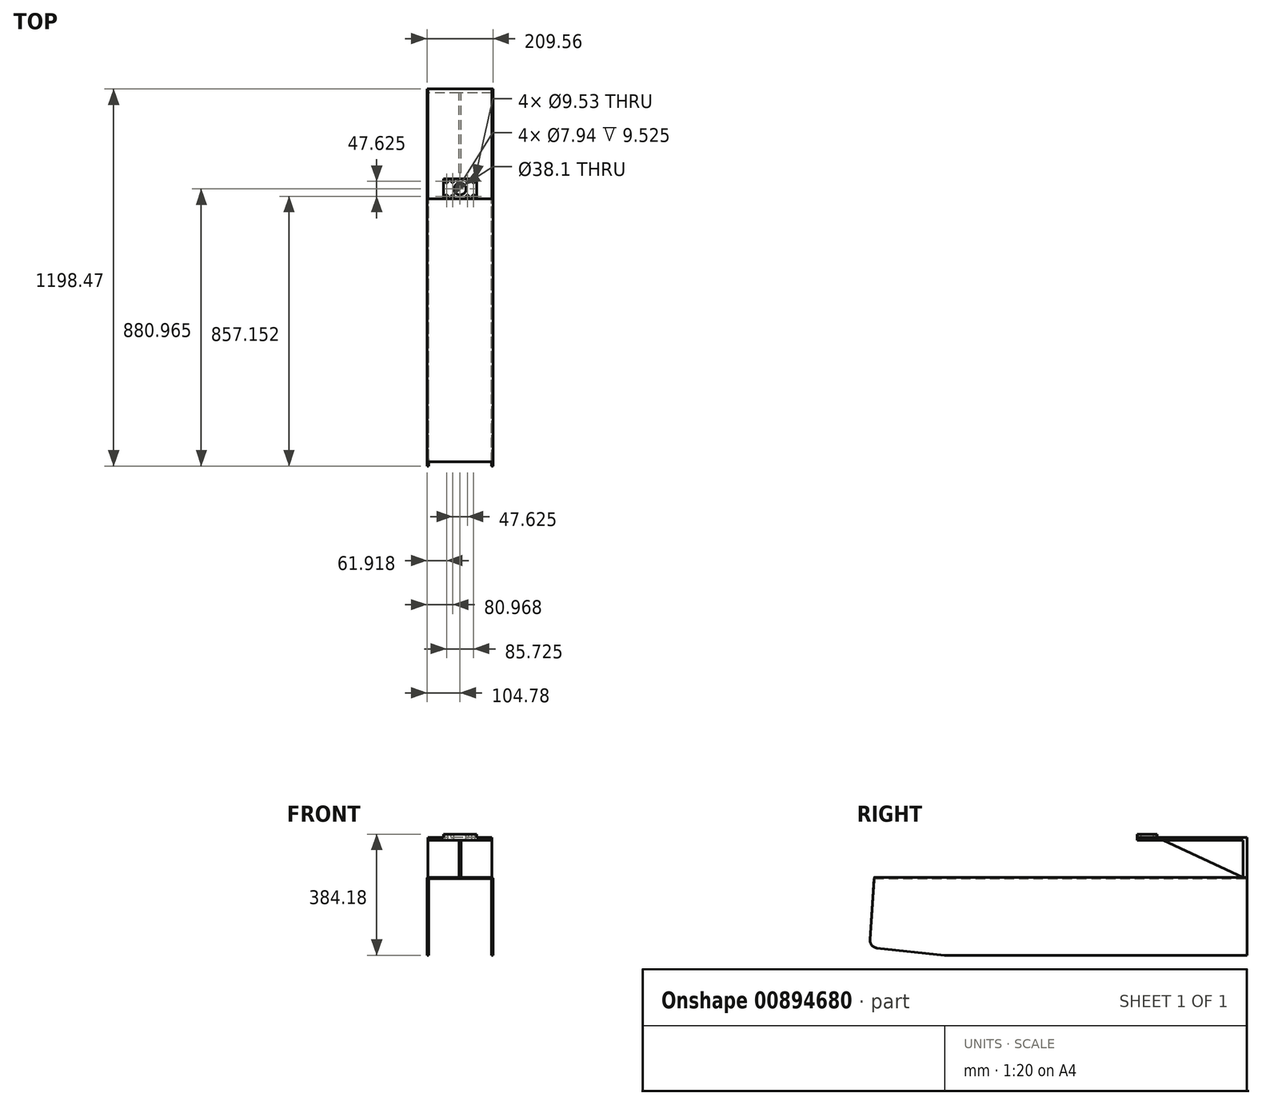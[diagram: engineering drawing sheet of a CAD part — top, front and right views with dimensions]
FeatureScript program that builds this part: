
annotation { "Feature Type Name" : "Feature", "Feature Type Description" : "" }
export const myFeature = defineFeature(function(context is Context, id is Id, definition is map)
    precondition{}
    {
        {
            var Q0;
            Q0=qCreatedBy(makeId("Front.planeOp"),FACE);
            var sketch = newSketch(context, id + "F0", { "sketchPlane" : qUnion([Q0])});
            skLineSegment(sketch, "E0", {"start": v(-100.01, -242.89) * mm, "end": v(-100.01, 0) * mm});
            skLineSegment(sketch, "E1", {"start": v(-100.01, 0) * mm, "end": v(100.01, 0) * mm});
            skLineSegment(sketch, "E2", {"start": v(100.01, 0) * mm, "end": v(100.01, -242.89) * mm});
            skLineSegment(sketch, "E3", {"start": v(-100.01, -242.89) * mm, "end": v(-104.78, -242.89) * mm});
            skLineSegment(sketch, "E4", {"start": v(-104.78, -242.89) * mm, "end": v(-104.78, 4.76) * mm});
            skLineSegment(sketch, "E5", {"start": v(-104.78, 4.76) * mm, "end": v(104.78, 4.76) * mm});
            skLineSegment(sketch, "E6", {"start": v(104.78, 4.76) * mm, "end": v(104.78, -242.89) * mm});
            skLineSegment(sketch, "E7", {"start": v(104.78, -242.89) * mm, "end": v(100.01, -242.89) * mm});
            skSolve(sketch);
        }
        {
            var Q0;
            Q0 = qSketchRegion(id + "F0", true);
            extrude(context, id + "F1", {"entities" : qUnion([Q0]), "endBound" : BoundingType.SYMMETRIC, "depth" : 1200.15 * mm, "offsetDistance" : 25.4 * mm});
        }
        {
            var Q0;
            Q0=makeQuery(id+"F1.opExtrude","SWEPT_EDGE",EDGE,{"disambiguationData":[OSD([sQuery(id+"F0.wireOp",EDGE,"E4"),sQuery(id+"F0.wireOp",EDGE,"E5")])]});
            var Q1;
            Q1=makeQuery(id+"F1.opExtrude","SWEPT_EDGE",EDGE,{"disambiguationData":[OSD([sQuery(id+"F0.wireOp",EDGE,"E0"),sQuery(id+"F0.wireOp",EDGE,"E1")])]});
            var Q2;
            Q2=makeQuery(id+"F1.opExtrude","SWEPT_EDGE",EDGE,{"disambiguationData":[OSD([sQuery(id+"F0.wireOp",EDGE,"E5"),sQuery(id+"F0.wireOp",EDGE,"E6")])]});
            var Q3;
            Q3=makeQuery(id+"F1.opExtrude","SWEPT_EDGE",EDGE,{"disambiguationData":[OSD([sQuery(id+"F0.wireOp",EDGE,"E1"),sQuery(id+"F0.wireOp",EDGE,"E2")])]});
            fillet(context, id + "F2", {"entities" : qUnion([Q0, Q1, Q2, Q3]), "radius" : 4.76 * mm, "tangentPropagation" : true, "allowEdgeOverflow" : false});
        }
        {
            var Q0;
            Q0=makeQuery(id+"F1.opExtrude","SWEPT_FACE",FACE,{"disambiguationData":[OSD([sQuery(id+"F0.wireOp",EDGE,"E4")])]});
            var sketch = newSketch(context, id + "F3", { "sketchPlane" : qUnion([Q0])});
            skLineSegment(sketch, "E8", {"start": v(600.08, -217.49) * mm, "end": v(361.95, -242.89) * mm});
            skLineSegment(sketch, "E9", {"start": v(361.95, -242.89) * mm, "end": v(600.08, -242.89) * mm});
            skLineSegment(sketch, "E10", {"start": v(600.08, -242.89) * mm, "end": v(600.08, -217.49) * mm});
            skLineSegment(sketch, "E11", {"start": v(584.2, 4.76) * mm, "end": v(600.08, 4.76) * mm});
            skSolve(sketch);
        }
        {
            var Q0;
            Q0 = qSketchRegion(id + "F3", true);
            var Q1;
            Q1=makeQuery(id+"F1.opExtrude","SWEPT_FACE",FACE,{"disambiguationData":[OSD([sQuery(id+"F0.wireOp",EDGE,"E6")])]});
            extrude(context, id + "F4", {"entities" : qUnion([Q0]), "operationType" : NewBodyOperationType.REMOVE, "endBound" : BoundingType.UP_TO_SURFACE, "oppositeDirection" : true, "depth" : 25.4 * mm, "endBoundEntityFace" : qUnion([Q1]), "offsetDistance" : 25.4 * mm});
        }
        {
            var Q0;
            Q0=makeQuery(id+"F1.opExtrude","SWEPT_FACE",FACE,{"disambiguationData":[OSD([sQuery(id+"F0.wireOp",EDGE,"E4")])]});
            var sketch = newSketch(context, id + "F5", { "sketchPlane" : qUnion([Q0])});
            skLineSegment(sketch, "E12", {"start": v(600.08, -217.49) * mm, "end": v(600.08, 4.76) * mm});
            skLineSegment(sketch, "E13", {"start": v(600.08, 4.76) * mm, "end": v(584.2, 4.76) * mm});
            skLineSegment(sketch, "E14", {"start": v(584.2, 4.76) * mm, "end": v(600.08, -217.49) * mm});
            skSolve(sketch);
        }
        {
            var Q0;
            Q0 = qSketchRegion(id + "F5", true);
            var Q1;
            Q1=makeQuery(id+"F1.opExtrude","SWEPT_FACE",FACE,{"disambiguationData":[OSD([sQuery(id+"F0.wireOp",EDGE,"E6")])]});
            extrude(context, id + "F6", {"entities" : qUnion([Q0]), "operationType" : NewBodyOperationType.REMOVE, "endBound" : BoundingType.UP_TO_SURFACE, "oppositeDirection" : true, "depth" : 25.4 * mm, "endBoundEntityFace" : qUnion([Q1]), "offsetDistance" : 25.4 * mm});
        }
        {
            var Q0;
            {var subQ0=sQuery(id+"F3.wireOp",EDGE,"E8");var subQ1=sQuery(id+"F0.wireOp",EDGE,"E0");var subQ2=sQuery(id+"F0.wireOp",EDGE,"E4");Q0=makeQuery(id+"F6.boolean.opBoolean","MERGE",EDGE,{"derivedFrom":[makeQuery(id+"F4.boolean.opBoolean","COPY",EDGE,{"disambiguationData":[TD([makeQuery(id+"F1.opExtrude","SWEPT_FACE",FACE,{"disambiguationData":[OSD([subQ1])]})])],"derivedFrom":makeQuery(id+"F4.opExtrude","SWEPT_EDGE",EDGE,{"disambiguationData":[OSD([subQ2,subQ0,sQuery(id+"F3.wireOp",EDGE,"E10")])]})})],"fromTools":[makeQuery(id+"F6.opExtrude","SWEPT_EDGE",EDGE,{"disambiguationData":[OSD([subQ0,sQuery(id+"F5.wireOp",EDGE,"E12"),sQuery(id+"F5.wireOp",EDGE,"E14")])]})]});}
            var Q1;
            {var subQ0=sQuery(id+"F3.wireOp",EDGE,"E8");var subQ2=sQuery(id+"F0.wireOp",EDGE,"E4");var subQ3=sQuery(id+"F0.wireOp",EDGE,"E2");Q1=makeQuery(id+"F6.boolean.opBoolean","MERGE",EDGE,{"derivedFrom":[makeQuery(id+"F4.boolean.opBoolean","COPY",EDGE,{"disambiguationData":[TD([makeQuery(id+"F1.opExtrude","SWEPT_FACE",FACE,{"disambiguationData":[OSD([subQ3])]})])],"derivedFrom":makeQuery(id+"F4.opExtrude","SWEPT_EDGE",EDGE,{"disambiguationData":[OSD([subQ2,subQ0,sQuery(id+"F3.wireOp",EDGE,"E10")])]})})],"fromTools":[makeQuery(id+"F6.opExtrude","SWEPT_EDGE",EDGE,{"disambiguationData":[OSD([subQ0,sQuery(id+"F5.wireOp",EDGE,"E12"),sQuery(id+"F5.wireOp",EDGE,"E14")])]})]});}
            var Q2;
            {var subQ0=sQuery(id+"F0.wireOp",EDGE,"E3");var subQ1=sQuery(id+"F3.wireOp",EDGE,"E8");Q2=makeQuery(id+"F4.boolean.opBoolean","COPY",EDGE,{"disambiguationData":[topologyDisambiguationEdgeConnected([makeQuery(id+"F1.opExtrude","SWEPT_FACE",FACE,{"disambiguationData":[OSD([subQ0])]})])],"derivedFrom":makeQuery(id+"F4.opExtrude","SWEPT_EDGE",EDGE,{"disambiguationData":[OSD([subQ0,sQuery(id+"F0.wireOp",EDGE,"E4"),subQ1,sQuery(id+"F3.wireOp",EDGE,"E9")])]})});}
            var Q3;
            {var subQ0=sQuery(id+"F3.wireOp",EDGE,"E8");Q3=makeQuery(id+"F4.boolean.opBoolean","COPY",EDGE,{"disambiguationData":[topologyDisambiguationEdgeConnected([makeQuery(id+"F1.opExtrude","SWEPT_FACE",FACE,{"disambiguationData":[OSD([sQuery(id+"F0.wireOp",EDGE,"E7")])]})])],"derivedFrom":makeQuery(id+"F4.opExtrude","SWEPT_EDGE",EDGE,{"disambiguationData":[OSD([sQuery(id+"F0.wireOp",EDGE,"E3"),sQuery(id+"F0.wireOp",EDGE,"E4"),subQ0,sQuery(id+"F3.wireOp",EDGE,"E9")])]})});}
            fillet(context, id + "F7", {"entities" : qUnion([Q0, Q1, Q2, Q3]), "radius" : 25.4 * mm, "tangentPropagation" : true, "allowEdgeOverflow" : false});
        }
        {
            var Q0;
            Q0=qCreatedBy(makeId("Right.planeOp"),FACE);
            var sketch = newSketch(context, id + "F8", { "sketchPlane" : qUnion([Q0])});
            skLineSegment(sketch, "E15", {"start": v(600.08, 4.76) * mm, "end": v(600.08, 131.76) * mm});
            skLineSegment(sketch, "E16", {"start": v(600.08, 131.76) * mm, "end": v(250.82, 131.76) * mm});
            skLineSegment(sketch, "E17", {"start": v(250.82, 131.76) * mm, "end": v(250.82, 122.24) * mm});
            skLineSegment(sketch, "E18", {"start": v(250.82, 122.24) * mm, "end": v(587.38, 122.24) * mm});
            skLineSegment(sketch, "E19", {"start": v(587.38, 122.24) * mm, "end": v(587.38, 4.76) * mm});
            skLineSegment(sketch, "E20", {"start": v(587.38, 4.76) * mm, "end": v(600.08, 4.76) * mm});
            skSolve(sketch);
        }
        {
            var Q0;
            Q0 = qSketchRegion(id + "F8", true);
            extrude(context, id + "F9", {"entities" : qUnion([Q0]), "operationType" : NewBodyOperationType.ADD, "endBound" : BoundingType.SYMMETRIC, "depth" : 203.2 * mm, "offsetDistance" : 25.4 * mm});
        }
        {
            var Q0;
            Q0=qCreatedBy(makeId("Right.planeOp"),FACE);
            var sketch = newSketch(context, id + "F10", { "sketchPlane" : qUnion([Q0])});
            skLineSegment(sketch, "E21", {"start": v(587.38, 122.24) * mm, "end": v(587.38, 4.76) * mm});
            skLineSegment(sketch, "E22", {"start": v(587.38, 4.76) * mm, "end": v(333.37, 122.24) * mm});
            skLineSegment(sketch, "E23", {"start": v(333.38, 122.24) * mm, "end": v(587.38, 122.24) * mm});
            skSolve(sketch);
        }
        {
            var Q0;
            Q0 = qSketchRegion(id + "F10", true);
            extrude(context, id + "F11", {"entities" : qUnion([Q0]), "operationType" : NewBodyOperationType.ADD, "endBound" : BoundingType.SYMMETRIC, "depth" : 6.35 * mm, "offsetDistance" : 25.4 * mm});
        }
        {
            var Q0;
            Q0=makeQuery(id+"F9.opExtrude","SWEPT_FACE",FACE,{"disambiguationData":[OSD([sQuery(id+"F8.wireOp",EDGE,"E16")])]});
            var sketch = newSketch(context, id + "F12", { "sketchPlane" : qUnion([Q0])});
            skLineSegment(sketch, "E24.bottom", {"start": v(52.39, 314.32) * mm, "end": v(-52.39, 314.32) * mm});
            skLineSegment(sketch, "E24.top", {"start": v(52.39, 250.82) * mm, "end": v(-52.39, 250.82) * mm});
            skLineSegment(sketch, "E24.left", {"start": v(52.39, 314.32) * mm, "end": v(52.39, 250.82) * mm});
            skLineSegment(sketch, "E24.right", {"start": v(-52.39, 314.32) * mm, "end": v(-52.39, 250.82) * mm});
            skPoint(sketch, "E24.middle", {"position": v(0, 282.57) * mm});
            skSolve(sketch);
        }
        {
            var Q0;
            Q0 = qSketchRegion(id + "F12", true);
            extrude(context, id + "F13", {"entities" : qUnion([Q0]), "operationType" : NewBodyOperationType.ADD, "depth" : 9.52 * mm, "offsetDistance" : 25.4 * mm});
        }
        {
            var Q0;
            Q0=makeQuery(id+"F13.opExtrude","CAP_FACE",FACE,{"disambiguationData":[OSD([sQuery(id+"F12.wireOp",EDGE,"E24.bottom"),sQuery(id+"F12.wireOp",EDGE,"E24.top"),sQuery(id+"F12.wireOp",EDGE,"E24.left"),sQuery(id+"F12.wireOp",EDGE,"E24.right")])],"isStart":false});
            var sketch = newSketch(context, id + "F14", { "sketchPlane" : qUnion([Q0])});
            skCircle(sketch, "E25", {"center": v(0, 282.57) * mm, "radius": 19.05 * mm});
            skLineSegment(sketch, "E26.bottom", {"start": v(42.86, 306.39) * mm, "end": v(-42.86, 306.39) * mm, "construction": true});
            skLineSegment(sketch, "E26.top", {"start": v(42.86, 258.76) * mm, "end": v(-42.86, 258.76) * mm, "construction": true});
            skLineSegment(sketch, "E26.left", {"start": v(42.86, 306.39) * mm, "end": v(42.86, 258.76) * mm, "construction": true});
            skLineSegment(sketch, "E26.right", {"start": v(-42.86, 306.39) * mm, "end": v(-42.86, 258.76) * mm, "construction": true});
            skCircle(sketch, "E27", {"center": v(-42.86, 306.39) * mm, "radius": 4.76 * mm});
            skCircle(sketch, "E28", {"center": v(-42.86, 258.76) * mm, "radius": 4.76 * mm});
            skCircle(sketch, "E29", {"center": v(42.86, 258.76) * mm, "radius": 4.76 * mm});
            skCircle(sketch, "E30", {"center": v(42.86, 306.39) * mm, "radius": 4.76 * mm});
            skSolve(sketch);
        }
        {
            var Q0;
            Q0 = qSketchRegion(id + "F14", true);
            extrude(context, id + "F15", {"entities" : qUnion([Q0]), "operationType" : NewBodyOperationType.REMOVE, "endBound" : BoundingType.UP_TO_NEXT, "oppositeDirection" : true, "depth" : 25.4 * mm, "offsetDistance" : 25.4 * mm});
        }
        {
            var Q0;
            Q0=makeQuery(id+"F13.opExtrude","CAP_FACE",FACE,{"disambiguationData":[OSD([sQuery(id+"F12.wireOp",EDGE,"E24.bottom"),sQuery(id+"F12.wireOp",EDGE,"E24.top"),sQuery(id+"F12.wireOp",EDGE,"E24.left"),sQuery(id+"F12.wireOp",EDGE,"E24.right")])],"isStart":false});
            var sketch = newSketch(context, id + "F16", { "sketchPlane" : qUnion([Q0])});
            skLineSegment(sketch, "E31.bottom", {"start": v(23.81, 306.39) * mm, "end": v(-23.81, 306.39) * mm, "construction": true});
            skLineSegment(sketch, "E31.top", {"start": v(23.81, 258.76) * mm, "end": v(-23.81, 258.76) * mm, "construction": true});
            skLineSegment(sketch, "E31.left", {"start": v(23.81, 306.39) * mm, "end": v(23.81, 258.76) * mm, "construction": true});
            skLineSegment(sketch, "E31.right", {"start": v(-23.81, 306.39) * mm, "end": v(-23.81, 258.76) * mm, "construction": true});
            skPoint(sketch, "E31.middle", {"position": v(0, 282.57) * mm});
            skCircle(sketch, "E32", {"center": v(-23.81, 306.39) * mm, "radius": 3.97 * mm});
            skCircle(sketch, "E33", {"center": v(23.81, 306.39) * mm, "radius": 3.97 * mm});
            skCircle(sketch, "E34", {"center": v(23.81, 258.76) * mm, "radius": 3.97 * mm});
            skCircle(sketch, "E35", {"center": v(-23.81, 258.76) * mm, "radius": 3.97 * mm});
            skSolve(sketch);
        }
        {
            var Q0;
            Q0 = qSketchRegion(id + "F16", true);
            var Q1;
            Q1=makeQuery(id+"F9.opExtrude","SWEPT_FACE",FACE,{"disambiguationData":[OSD([sQuery(id+"F8.wireOp",EDGE,"E16")])]});
            extrude(context, id + "F17", {"entities" : qUnion([Q0]), "operationType" : NewBodyOperationType.REMOVE, "endBound" : BoundingType.UP_TO_SURFACE, "oppositeDirection" : true, "depth" : 25.4 * mm, "endBoundEntityFace" : qUnion([Q1]), "offsetDistance" : 25.4 * mm});
        }
    });
